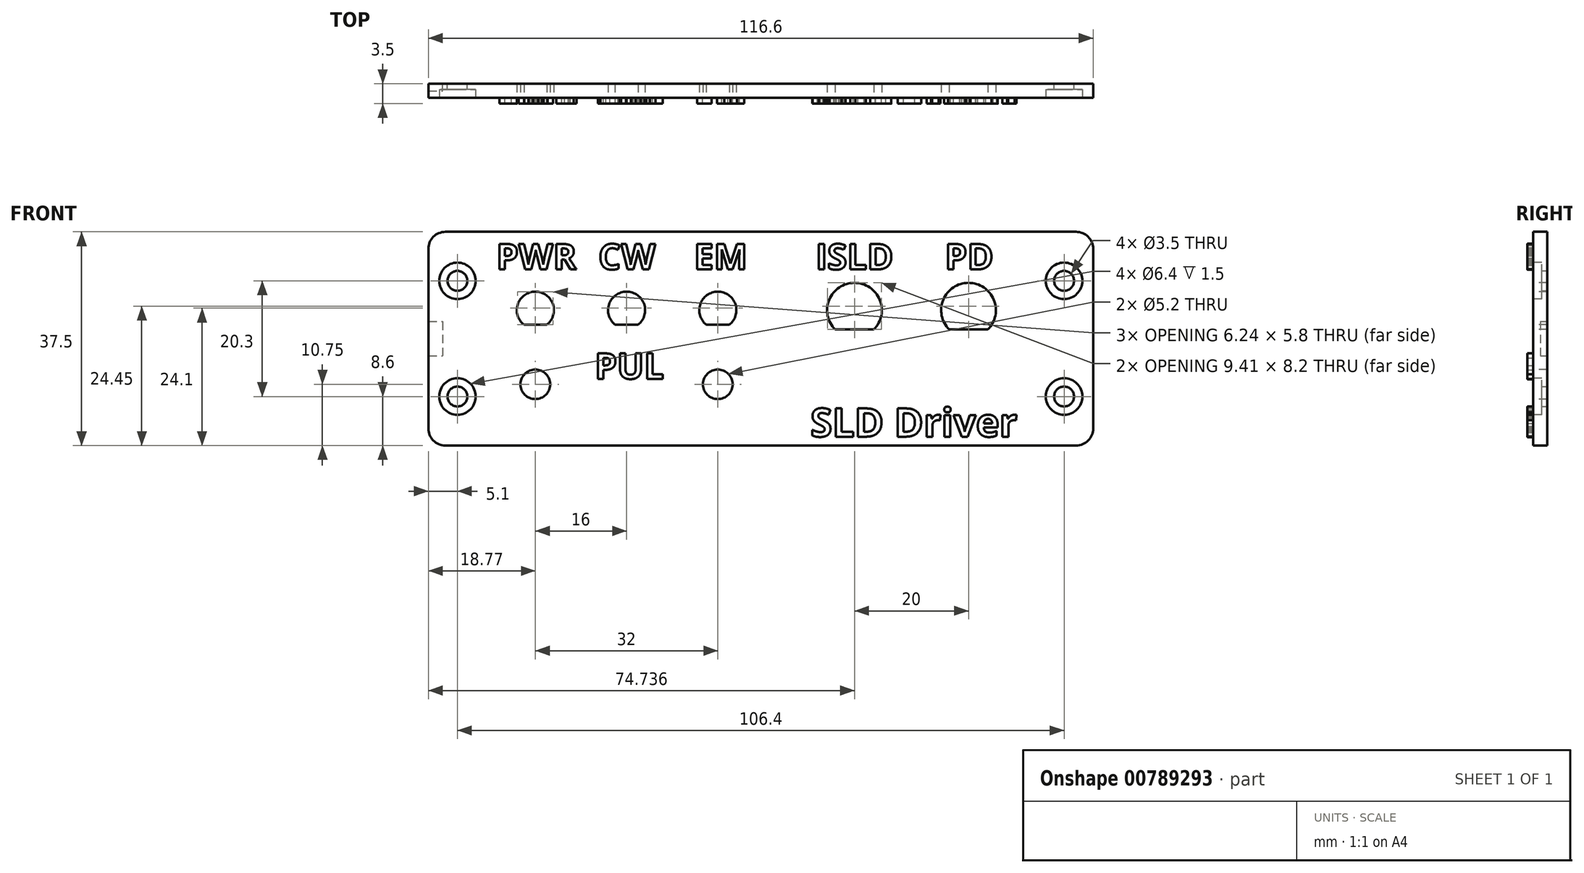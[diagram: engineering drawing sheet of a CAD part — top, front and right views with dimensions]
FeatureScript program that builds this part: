
annotation { "Feature Type Name" : "Feature", "Feature Type Description" : "" }
export const myFeature = defineFeature(function(context is Context, id is Id, definition is map)
    precondition{}
    {
        {
            var Q0;
            Q0=qCreatedBy(makeId("Front.planeOp"),FACE);
            var sketch = newSketch(context, id + "F0", { "sketchPlane" : qUnion([Q0])});
            skLineSegment(sketch, "E0.bottom", {"start": v(-55.3, 18.75) * mm, "end": v(55.3, 18.75) * mm});
            skLineSegment(sketch, "E0.top", {"start": v(-55.3, -18.75) * mm, "end": v(55.3, -18.75) * mm});
            skLineSegment(sketch, "E0.left", {"start": v(-58.3, 15.75) * mm, "end": v(-58.3, -15.75) * mm});
            skLineSegment(sketch, "E0.right", {"start": v(58.3, 15.75) * mm, "end": v(58.3, -15.75) * mm});
            skPoint(sketch, "E1.visualSharp", {"position": v(-58.3, 18.75) * mm});
            skArc(sketch, "E1.filletArc", {"start": v(-55.3, 18.75) * mm, "mid": v(-57.42, 17.87) * mm, "end": v(-58.3, 15.75) * mm});
            skPoint(sketch, "E2.visualSharp", {"position": v(58.3, 18.75) * mm});
            skArc(sketch, "E2.filletArc", {"start": v(58.3, 15.75) * mm, "mid": v(57.42, 17.87) * mm, "end": v(55.3, 18.75) * mm});
            skPoint(sketch, "E3.visualSharp", {"position": v(58.3, -18.75) * mm});
            skArc(sketch, "E3.filletArc", {"start": v(55.3, -18.75) * mm, "mid": v(57.42, -17.87) * mm, "end": v(58.3, -15.75) * mm});
            skPoint(sketch, "E4.visualSharp", {"position": v(-58.3, -18.75) * mm});
            skArc(sketch, "E4.filletArc", {"start": v(-58.3, -15.75) * mm, "mid": v(-57.42, -17.87) * mm, "end": v(-55.3, -18.75) * mm});
            skCircle(sketch, "E5", {"center": v(-53.2, 10.15) * mm, "radius": 1.75 * mm});
            skCircle(sketch, "E6", {"center": v(53.2, 10.15) * mm, "radius": 1.75 * mm});
            skCircle(sketch, "E7", {"center": v(-53.2, -10.15) * mm, "radius": 1.75 * mm});
            skCircle(sketch, "E8", {"center": v(53.2, -10.15) * mm, "radius": 1.75 * mm});
            skSolve(sketch);
        }
        {
            var Q0;
            Q0=makeQuery(id+"F0.imprint","IMPRINT",FACE,{"disambiguationData":[TD([[makeQuery(id+"F0.imprint","IMPRINT",EDGE,{"derivedFrom":sQuery(id+"F0.wireOp",EDGE,"E0.bottom")}),-1.0]])]});
            extrude(context, id + "F1", {"entities" : qUnion([Q0]), "depth" : 2.5 * mm});
        }
        {
            var Q0;
            Q0=makeQuery(id+"F1.opExtrude","CAP_FACE",FACE,{"disambiguationData":[OSD([sQuery(id+"F0.wireOp",EDGE,"E0.bottom"),sQuery(id+"F0.wireOp",EDGE,"E0.top"),sQuery(id+"F0.wireOp",EDGE,"E0.left"),sQuery(id+"F0.wireOp",EDGE,"E0.right"),sQuery(id+"F0.wireOp",EDGE,"E1.filletArc"),sQuery(id+"F0.wireOp",EDGE,"E2.filletArc"),sQuery(id+"F0.wireOp",EDGE,"E3.filletArc"),sQuery(id+"F0.wireOp",EDGE,"E4.filletArc"),sQuery(id+"F0.wireOp",EDGE,"E5"),sQuery(id+"F0.wireOp",EDGE,"E6"),sQuery(id+"F0.wireOp",EDGE,"E7"),sQuery(id+"F0.wireOp",EDGE,"E8")])],"isStart":false});
            var sketch = newSketch(context, id + "F2", { "sketchPlane" : qUnion([Q0])});
            skCircle(sketch, "E9", {"center": v(-53.2, 10.15) * mm, "radius": 3.2 * mm});
            skCircle(sketch, "E10", {"center": v(53.2, 10.15) * mm, "radius": 3.2 * mm});
            skCircle(sketch, "E11", {"center": v(-53.2, -10.15) * mm, "radius": 3.2 * mm});
            skCircle(sketch, "E12", {"center": v(53.2, -10.15) * mm, "radius": 3.2 * mm});
            skSolve(sketch);
        }
        {
            var Q0;
            Q0=qSketchRegion(id+"F2",true);
            extrude(context, id + "F3", {"entities" : qUnion([Q0]), "operationType" : NewBodyOperationType.REMOVE, "oppositeDirection" : true, "depth" : 1.5 * mm});
        }
        {
            var Q0;
            Q0=makeQuery(id+"F1.opExtrude","CAP_FACE",FACE,{"disambiguationData":[OSD([sQuery(id+"F0.wireOp",EDGE,"E0.bottom"),sQuery(id+"F0.wireOp",EDGE,"E0.top"),sQuery(id+"F0.wireOp",EDGE,"E0.left"),sQuery(id+"F0.wireOp",EDGE,"E0.right"),sQuery(id+"F0.wireOp",EDGE,"E1.filletArc"),sQuery(id+"F0.wireOp",EDGE,"E2.filletArc"),sQuery(id+"F0.wireOp",EDGE,"E3.filletArc"),sQuery(id+"F0.wireOp",EDGE,"E4.filletArc"),sQuery(id+"F0.wireOp",EDGE,"E5"),sQuery(id+"F0.wireOp",EDGE,"E6"),sQuery(id+"F0.wireOp",EDGE,"E7"),sQuery(id+"F0.wireOp",EDGE,"E8")])],"isStart":true});
            var sketch = newSketch(context, id + "F4", { "sketchPlane" : qUnion([Q0])});
            skLineSegment(sketch, "E13.bottom", {"start": v(58.3, 3) * mm, "end": v(55.8, 3) * mm});
            skLineSegment(sketch, "E13.top", {"start": v(58.3, -3) * mm, "end": v(55.8, -3) * mm});
            skLineSegment(sketch, "E13.left", {"start": v(58.3, 3) * mm, "end": v(58.3, -3) * mm});
            skLineSegment(sketch, "E13.right", {"start": v(55.8, 3) * mm, "end": v(55.8, -3) * mm});
            skSolve(sketch);
        }
        {
            var Q0;
            Q0=qSketchRegion(id+"F4",true);
            extrude(context, id + "F5", {"entities" : qUnion([Q0]), "operationType" : NewBodyOperationType.REMOVE, "oppositeDirection" : true, "depth" : 1.25 * mm});
        }
        {
            var Q0;
            Q0=makeQuery(id+"F1.opExtrude","CAP_FACE",FACE,{"disambiguationData":[OSD([sQuery(id+"F0.wireOp",EDGE,"E0.bottom"),sQuery(id+"F0.wireOp",EDGE,"E0.top"),sQuery(id+"F0.wireOp",EDGE,"E0.left"),sQuery(id+"F0.wireOp",EDGE,"E0.right"),sQuery(id+"F0.wireOp",EDGE,"E1.filletArc"),sQuery(id+"F0.wireOp",EDGE,"E2.filletArc"),sQuery(id+"F0.wireOp",EDGE,"E3.filletArc"),sQuery(id+"F0.wireOp",EDGE,"E4.filletArc"),sQuery(id+"F0.wireOp",EDGE,"E5"),sQuery(id+"F0.wireOp",EDGE,"E6"),sQuery(id+"F0.wireOp",EDGE,"E7"),sQuery(id+"F0.wireOp",EDGE,"E8")])],"isStart":false});
            var sketch = newSketch(context, id + "F6", { "sketchPlane" : qUnion([Q0])});
            skLineSegment(sketch, "E14", {"start": v(-63.46, 5) * mm, "end": v(64.15, 5) * mm, "construction": true});
            skArc(sketch, "E15", {"start": v(-37.52, 2.45) * mm, "mid": v(-39.53, 8.25) * mm, "end": v(-41.55, 2.45) * mm});
            skArc(sketch, "E16", {"start": v(-21.52, 2.45) * mm, "mid": v(-23.53, 8.25) * mm, "end": v(-25.55, 2.45) * mm});
            skArc(sketch, "E17", {"start": v(-5.52, 2.45) * mm, "mid": v(-7.53, 8.25) * mm, "end": v(-9.55, 2.45) * mm});
            skArc(sketch, "E18", {"start": v(39.82, 1.6) * mm, "mid": v(36.44, 9.8) * mm, "end": v(33.05, 1.6) * mm});
            skArc(sketch, "E19", {"start": v(19.82, 1.6) * mm, "mid": v(16.44, 9.8) * mm, "end": v(13.05, 1.6) * mm});
            skLineSegment(sketch, "E20", {"start": v(-48.3, 18.75) * mm, "end": v(-48.3, -12.75) * mm, "construction": true});
            skLineSegment(sketch, "E21", {"start": v(-48.3, -12.75) * mm, "end": v(48.3, -12.75) * mm, "construction": true});
            skLineSegment(sketch, "E22", {"start": v(48.3, -12.75) * mm, "end": v(48.3, 18.75) * mm, "construction": true});
            skLineSegment(sketch, "E23", {"start": v(-41.55, 2.45) * mm, "end": v(-37.52, 2.45) * mm});
            skLineSegment(sketch, "E24.trimOffspring", {"start": v(-25.55, 2.45) * mm, "end": v(-21.52, 2.45) * mm});
            skLineSegment(sketch, "E25.trimOffspring", {"start": v(-9.55, 2.45) * mm, "end": v(-5.52, 2.45) * mm});
            skLineSegment(sketch, "E26", {"start": v(13.05, 1.6) * mm, "end": v(19.82, 1.6) * mm});
            skLineSegment(sketch, "E27.trimOffspring", {"start": v(33.05, 1.6) * mm, "end": v(39.82, 1.6) * mm});
            skLineSegment(sketch, "E28", {"start": v(11.1, 9.8) * mm, "end": v(46.97, 9.8) * mm, "construction": true});
            skLineSegment(sketch, "E29", {"start": v(-42.3, 8.25) * mm, "end": v(6.57, 8.25) * mm, "construction": true});
            skCircle(sketch, "E30", {"center": v(-39.53, -8) * mm, "radius": 2.6 * mm});
            skCircle(sketch, "E31", {"center": v(-7.53, -8) * mm, "radius": 2.6 * mm});
            skLineSegment(sketch, "E32", {"start": v(-63, -8) * mm, "end": v(6.15, -8) * mm, "construction": true});
            skSolve(sketch);
        }
        {
            var Q0;
            Q0=qSketchRegion(id+"F6",true);
            extrude(context, id + "F7", {"entities" : qUnion([Q0]), "operationType" : NewBodyOperationType.REMOVE, "endBound" : BoundingType.THROUGH_ALL, "oppositeDirection" : true, "depth" : 25 * mm});
        }
        {
            var Q0;
            Q0=makeQuery(id+"F1.opExtrude","CAP_FACE",FACE,{"disambiguationData":[OSD([sQuery(id+"F0.wireOp",EDGE,"E0.bottom"),sQuery(id+"F0.wireOp",EDGE,"E0.top"),sQuery(id+"F0.wireOp",EDGE,"E0.left"),sQuery(id+"F0.wireOp",EDGE,"E0.right"),sQuery(id+"F0.wireOp",EDGE,"E1.filletArc"),sQuery(id+"F0.wireOp",EDGE,"E2.filletArc"),sQuery(id+"F0.wireOp",EDGE,"E3.filletArc"),sQuery(id+"F0.wireOp",EDGE,"E4.filletArc"),sQuery(id+"F0.wireOp",EDGE,"E5"),sQuery(id+"F0.wireOp",EDGE,"E6"),sQuery(id+"F0.wireOp",EDGE,"E7"),sQuery(id+"F0.wireOp",EDGE,"E8")])],"isStart":false});
            var sketch = newSketch(context, id + "F8", { "sketchPlane" : qUnion([Q0])});
            skText(sketch, "E33", { "text": "PWR", "fontName": "OpenSans-Bold.ttf"});
            skLineSegment(sketch, "E34", {"start": v(-84.62, 12.15) * mm, "end": v(84.91, 12.15) * mm, "construction": true});
            skText(sketch, "E35", { "text": "CW", "fontName": "OpenSans-Bold.ttf"});
            skText(sketch, "E36", { "text": "EM", "fontName": "OpenSans-Bold.ttf"});
            skText(sketch, "E37", { "text": "ISLD", "fontName": "OpenSans-Bold.ttf"});
            skText(sketch, "E38", { "text": "PD", "fontName": "OpenSans-Bold.ttf"});
            const initialGuessF8  = {"E33": [-0.0464, 0.01215, 1, 0, 0.0045], "E35": [-0.0285, 0.01215, 1, 0, 0.0045], "E36": [-0.01172, 0.01215, 1, 0, 0.0045], "E37": [0.0096, 0.01215, 1, 0, 0.0045], "E38": [0.03227, 0.01215, 1, 0, 0.0045]};
            skSetInitialGuess(sketch, initialGuessF8);
            skSolve(sketch);
        }
        {
            var Q0;
            Q0=qSketchRegion(id+"F8",true);
            extrude(context, id + "F9", {"entities" : qUnion([Q0]), "operationType" : NewBodyOperationType.ADD, "depth" : 1 * mm});
        }
        {
            var Q0;
            {var subQ0=sQuery(id+"F0.wireOp",EDGE,"E0.right");var subQ1=sQuery(id+"F0.wireOp",EDGE,"E3.filletArc");var subQ2=sQuery(id+"F0.wireOp",EDGE,"E4.filletArc");var subQ3=sQuery(id+"F0.wireOp",EDGE,"E1.filletArc");var subQ4=sQuery(id+"F0.wireOp",EDGE,"E0.top");var subQ5=sQuery(id+"F0.wireOp",EDGE,"E0.left");var subQ6=sQuery(id+"F0.wireOp",EDGE,"E2.filletArc");var subQ7=sQuery(id+"F0.wireOp",EDGE,"E0.bottom");Q0=makeQuery(id+"F9.boolean.opBoolean","SPLIT",FACE,{"disambiguationData":[TD([makeQuery(id+"F1.opExtrude","SWEPT_FACE",FACE,{"disambiguationData":[OSD([subQ7])]})])],"derivedFrom":makeQuery(id+"F1.opExtrude","CAP_FACE",FACE,{"disambiguationData":[OSD([subQ7,subQ4,subQ5,subQ0,subQ3,subQ6,subQ1,subQ2,sQuery(id+"F0.wireOp",EDGE,"E5"),sQuery(id+"F0.wireOp",EDGE,"E6"),sQuery(id+"F0.wireOp",EDGE,"E7"),sQuery(id+"F0.wireOp",EDGE,"E8")])],"isStart":false})});}
            var sketch = newSketch(context, id + "F10", { "sketchPlane" : qUnion([Q0])});
            skText(sketch, "E39", { "text": "PUL", "fontName": "OpenSans-Bold.ttf"});
            const initialGuessF10  = {"E39": [-0.02913, -0.00705, 1, 0, 0.0045]};
            skSetInitialGuess(sketch, initialGuessF10);
            skSolve(sketch);
        }
        {
            var Q0;
            Q0=qSketchRegion(id+"F10",true);
            extrude(context, id + "F11", {"entities" : qUnion([Q0]), "operationType" : NewBodyOperationType.ADD, "depth" : 1 * mm});
        }
        {
            var Q0;
            {var subQ70=sQuery(id+"F0.wireOp",EDGE,"E0.right");var subQ114=sQuery(id+"F0.wireOp",EDGE,"E3.filletArc");var subQ120=sQuery(id+"F0.wireOp",EDGE,"E4.filletArc");var subQ132=sQuery(id+"F0.wireOp",EDGE,"E1.filletArc");var subQ140=sQuery(id+"F0.wireOp",EDGE,"E0.top");var subQ143=sQuery(id+"F0.wireOp",EDGE,"E0.left");var subQ152=sQuery(id+"F0.wireOp",EDGE,"E2.filletArc");var subQ182=sQuery(id+"F0.wireOp",EDGE,"E0.bottom");var subQ183=makeQuery(id+"F1.opExtrude","SWEPT_FACE",FACE,{"disambiguationData":[OSD([subQ182])]});Q0=makeQuery(id+"F11.boolean.opBoolean","SPLIT",FACE,{"disambiguationData":[TD([subQ183])],"derivedFrom":makeQuery(id+"F9.boolean.opBoolean","SPLIT",FACE,{"disambiguationData":[TD([subQ183])],"derivedFrom":makeQuery(id+"F1.opExtrude","CAP_FACE",FACE,{"disambiguationData":[OSD([subQ182,subQ140,subQ143,subQ70,subQ132,subQ152,subQ114,subQ120,sQuery(id+"F0.wireOp",EDGE,"E5"),sQuery(id+"F0.wireOp",EDGE,"E6"),sQuery(id+"F0.wireOp",EDGE,"E7"),sQuery(id+"F0.wireOp",EDGE,"E8")])],"isStart":false})})});}
            var sketch = newSketch(context, id + "F12", { "sketchPlane" : qUnion([Q0])});
            skText(sketch, "E40", { "text": "SLD Driver", "fontName": "OpenSans-Bold.ttf"});
            const initialGuessF12  = {"E40": [0.00869, -0.0172, 1, 0, 0.005]};
            skSetInitialGuess(sketch, initialGuessF12);
            skSolve(sketch);
        }
        {
            var Q0;
            Q0=qSketchRegion(id+"F12",true);
            extrude(context, id + "F13", {"entities" : qUnion([Q0]), "operationType" : NewBodyOperationType.ADD, "depth" : 1 * mm});
        }
    });
